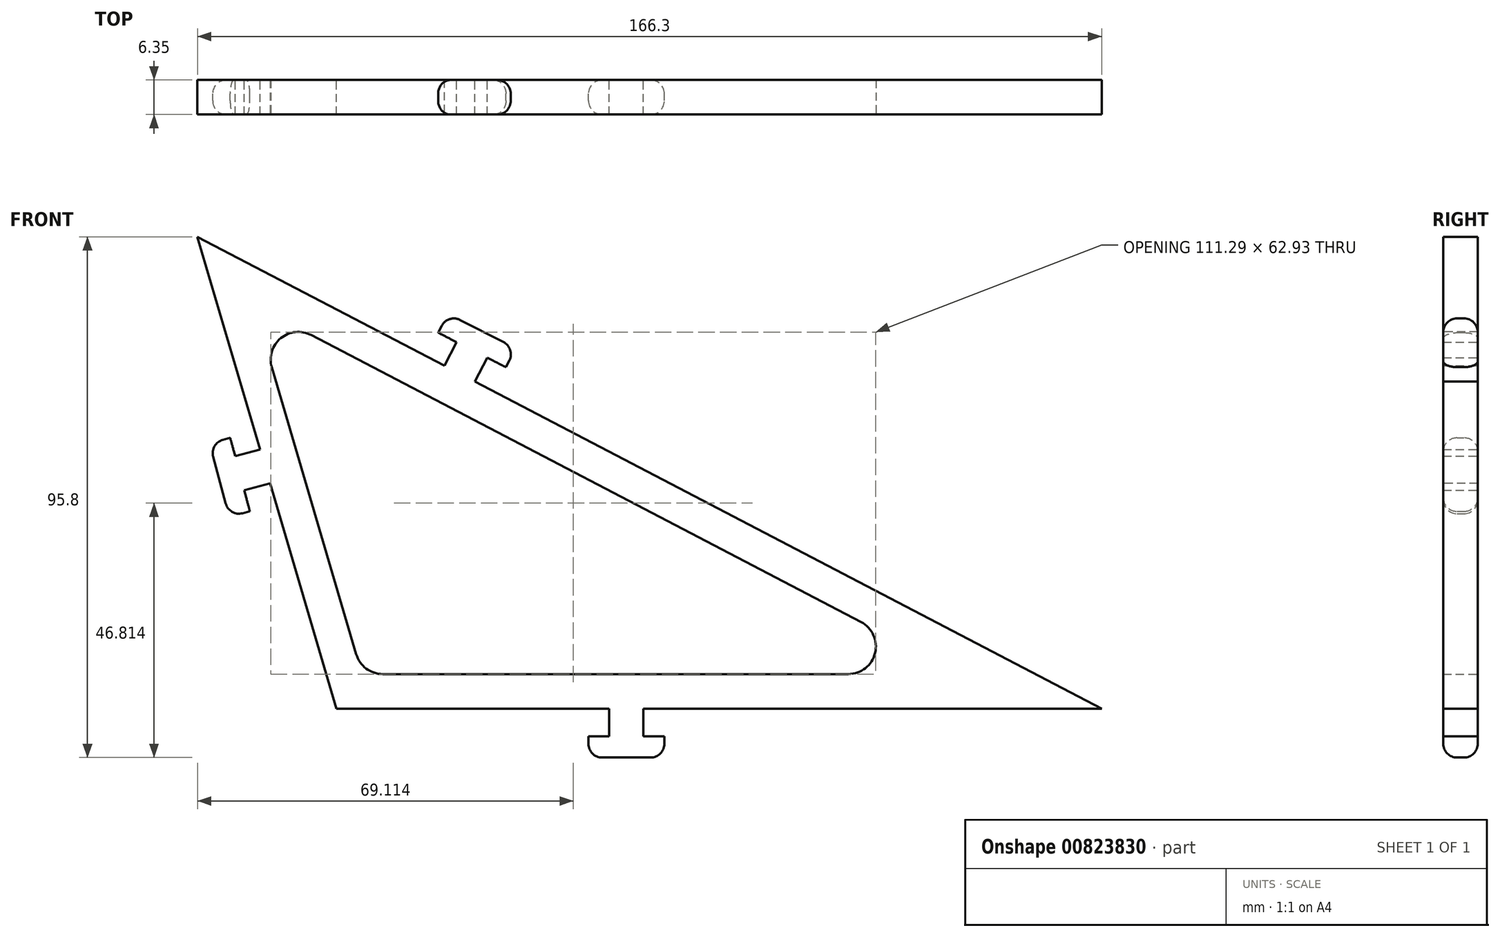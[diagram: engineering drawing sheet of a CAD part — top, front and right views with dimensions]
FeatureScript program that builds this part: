
annotation { "Feature Type Name" : "Feature", "Feature Type Description" : "" }
export const myFeature = defineFeature(function(context is Context, id is Id, definition is map)
    precondition{}
    {
        {
            var Q0;
            Q0=qCreatedBy(makeId("Front.planeOp"),FACE);
            var sketch = newSketch(context, id + "F0", { "sketchPlane" : qUnion([Q0])});
            skLineSegment(sketch, "E0", {"start": v(0, 0) * mm, "end": v(-140.78, 0) * mm});
            skLineSegment(sketch, "E1", {"start": v(-140.78, 0) * mm, "end": v(-166.3, 86.8) * mm});
            skLineSegment(sketch, "E2", {"start": v(-166.3, 86.8) * mm, "end": v(0, 0) * mm});
            skLineSegment(sketch, "E3.0", {"start": v(-156, 74.26) * mm, "end": v(-25.89, 6.35) * mm});
            skLineSegment(sketch, "E3.1", {"start": v(-136.03, 6.35) * mm, "end": v(-156, 74.26) * mm});
            skLineSegment(sketch, "E3.2", {"start": v(-25.89, 6.35) * mm, "end": v(-136.03, 6.35) * mm});
            skSolve(sketch);
        }
        {
            var Q0;
            Q0 = qSketchRegion(id + "F0", true);
            extrude(context, id + "F1", {"entities" : qUnion([Q0]), "depth" : 6.35 * mm, "offsetDistance" : 25.4 * mm});
        }
        {
            var Q0;
            Q0=makeQuery(id+"F1.opExtrude","SWEPT_EDGE",EDGE,{"disambiguationData":[OSD([sQuery(id+"F0.wireOp",EDGE,"E3.0"),sQuery(id+"F0.wireOp",EDGE,"E3.1")])]});
            var Q1;
            Q1=makeQuery(id+"F1.opExtrude","SWEPT_EDGE",EDGE,{"disambiguationData":[OSD([sQuery(id+"F0.wireOp",EDGE,"E3.0"),sQuery(id+"F0.wireOp",EDGE,"E3.2")])]});
            var Q2;
            Q2=makeQuery(id+"F1.opExtrude","SWEPT_EDGE",EDGE,{"disambiguationData":[OSD([sQuery(id+"F0.wireOp",EDGE,"E3.1"),sQuery(id+"F0.wireOp",EDGE,"E3.2")])]});
            fillet(context, id + "F2", {"entities" : qUnion([Q0, Q1, Q2]), "radius" : 5.08 * mm, "tangentPropagation" : true, "allowEdgeOverflow" : false});
        }
        {
            var Q0;
            Q0=qCreatedBy(makeId("Front.planeOp"),FACE);
            var sketch = newSketch(context, id + "F3", { "sketchPlane" : qUnion([Q0])});
            skLineSegment(sketch, "E4", {"start": v(-90.6, 0) * mm, "end": v(-90.6, -5.08) * mm});
            skLineSegment(sketch, "E5", {"start": v(-90.6, -5.08) * mm, "end": v(-94.4, -5.08) * mm});
            skLineSegment(sketch, "E6", {"start": v(-94.4, -5.08) * mm, "end": v(-94.4, -9) * mm});
            skLineSegment(sketch, "E7", {"start": v(-94.4, -9) * mm, "end": v(-80.42, -9) * mm});
            skLineSegment(sketch, "E8", {"start": v(-80.42, -9) * mm, "end": v(-80.42, -5.08) * mm});
            skLineSegment(sketch, "E9", {"start": v(-80.42, -5.08) * mm, "end": v(-84.3, -5.08) * mm});
            skLineSegment(sketch, "E10", {"start": v(-84.3, -5.08) * mm, "end": v(-84.3, 0) * mm});
            skLineSegment(sketch, "E11", {"start": v(-84.3, 0) * mm, "end": v(-90.6, 0) * mm});
            skSolve(sketch);
        }
        {
            var Q0;
            Q0=makeQuery(id+"F3.imprint","IMPRINT",FACE,{"disambiguationData":[TD([[makeQuery(id+"F3.imprint","IMPRINT",EDGE,{"derivedFrom":sQuery(id+"F3.wireOp",EDGE,"E4")}),1.0]])]});
            extrude(context, id + "F4", {"entities" : qUnion([Q0]), "operationType" : NewBodyOperationType.ADD, "depth" : 6.35 * mm, "offsetDistance" : 25.4 * mm});
        }
        {
            var Q0;
            Q0=makeQuery(id+"F4.opExtrude","CAP_EDGE",EDGE,{"disambiguationData":[OSD([sQuery(id+"F3.wireOp",EDGE,"E8")])],"isStart":true});
            fillet(context, id + "F5", {"entities" : qUnion([Q0]), "radius" : 2.54 * mm, "tangentPropagation" : true, "allowEdgeOverflow" : false});
        }
        {
            var Q0;
            Q0=makeQuery(id+"F4.opExtrude","CAP_EDGE",EDGE,{"disambiguationData":[OSD([sQuery(id+"F3.wireOp",EDGE,"E6")])],"isStart":true});
            fillet(context, id + "F6", {"entities" : qUnion([Q0]), "radius" : 2.54 * mm, "tangentPropagation" : true, "allowEdgeOverflow" : false});
        }
        {
            var Q0;
            Q0=makeQuery(id+"F4.opExtrude","CAP_EDGE",EDGE,{"disambiguationData":[OSD([sQuery(id+"F3.wireOp",EDGE,"E6")])],"isStart":false});
            var Q1;
            Q1=makeQuery(id+"F4.opExtrude","CAP_EDGE",EDGE,{"disambiguationData":[OSD([sQuery(id+"F3.wireOp",EDGE,"E8")])],"isStart":false});
            fillet(context, id + "F7", {"entities" : qUnion([Q0, Q1]), "radius" : 2.54 * mm, "tangentPropagation" : true, "allowEdgeOverflow" : false});
        }
        {
            var Q0;
            Q0=makeQuery(id+"F4.opExtrude","CAP_EDGE",EDGE,{"disambiguationData":[OSD([sQuery(id+"F3.wireOp",EDGE,"E7")])],"isStart":false});
            var Q1;
            Q1=makeQuery(id+"F4.opExtrude","CAP_EDGE",EDGE,{"disambiguationData":[OSD([sQuery(id+"F3.wireOp",EDGE,"E7")])],"isStart":true});
            fillet(context, id + "F8", {"entities" : qUnion([Q0, Q1]), "radius" : 2.54 * mm, "tangentPropagation" : true, "allowEdgeOverflow" : false});
        }
        {
            var Q0;
            Q0=makeQuery(id+"F4.boolean.opBoolean","MERGE",FACE,{"derivedFrom":[makeQuery(id+"F1.opExtrude","CAP_FACE",FACE,{"disambiguationData":[OSD([sQuery(id+"F0.wireOp",EDGE,"E0"),sQuery(id+"F0.wireOp",EDGE,"E1"),sQuery(id+"F0.wireOp",EDGE,"E2"),sQuery(id+"F0.wireOp",EDGE,"E3.0"),sQuery(id+"F0.wireOp",EDGE,"E3.1"),sQuery(id+"F0.wireOp",EDGE,"E3.2")])],"isStart":true}),makeQuery(id+"F4.opExtrude","CAP_FACE",FACE,{"disambiguationData":[OSD([sQuery(id+"F3.wireOp",EDGE,"E4"),sQuery(id+"F3.wireOp",EDGE,"E5"),sQuery(id+"F3.wireOp",EDGE,"E6"),sQuery(id+"F3.wireOp",EDGE,"E7"),sQuery(id+"F3.wireOp",EDGE,"E8"),sQuery(id+"F3.wireOp",EDGE,"E9"),sQuery(id+"F3.wireOp",EDGE,"E10"),sQuery(id+"F3.wireOp",EDGE,"E11")])],"isStart":true})]});
            var sketch = newSketch(context, id + "F9", { "sketchPlane" : qUnion([Q0])});
            skLineSegment(sketch, "E12", {"start": v(152.92, 41.46) * mm, "end": v(157.7, 40.18) * mm});
            skLineSegment(sketch, "E13", {"start": v(157.7, 40.18) * mm, "end": v(156.66, 36.3) * mm});
            skLineSegment(sketch, "E14", {"start": v(156.66, 36.3) * mm, "end": v(160.45, 35.29) * mm});
            skLineSegment(sketch, "E15", {"start": v(160.45, 35.29) * mm, "end": v(164.07, 48.8) * mm});
            skLineSegment(sketch, "E16", {"start": v(164.07, 48.8) * mm, "end": v(160.28, 49.81) * mm});
            skLineSegment(sketch, "E17", {"start": v(160.28, 49.81) * mm, "end": v(159.38, 46.45) * mm});
            skLineSegment(sketch, "E18", {"start": v(159.38, 46.45) * mm, "end": v(154.6, 47.73) * mm});
            skLineSegment(sketch, "E19", {"start": v(154.6, 47.73) * mm, "end": v(152.92, 41.46) * mm});
            skLineSegment(sketch, "E20.0", {"start": v(157.7, 40.18) * mm, "end": v(160.28, 49.81) * mm, "construction": true});
            skSolve(sketch);
        }
        {
            var Q0;
            {var subQ0=sQuery(id+"F9.wireOp",EDGE,"E19");Q0=makeQuery(id+"F9.imprint","IMPRINT",FACE,{"disambiguationData":[TD([[makeQuery(id+"F9.imprint","IMPRINT",EDGE,{"derivedFrom":subQ0}),1.0]])]});}
            var Q1;
            {var subQ0=sQuery(id+"F9.wireOp",EDGE,"E13");Q1=makeQuery(id+"F9.imprint","IMPRINT",FACE,{"disambiguationData":[TD([[makeQuery(id+"F9.imprint","IMPRINT",EDGE,{"derivedFrom":subQ0}),1.0]])]});}
            extrude(context, id + "F10", {"entities" : qUnion([Q0, Q1]), "operationType" : NewBodyOperationType.ADD, "oppositeDirection" : true, "depth" : 6.35 * mm, "offsetDistance" : 25.4 * mm});
        }
        {
            var Q0;
            Q0=makeQuery(id+"F10.opExtrude","CAP_EDGE",EDGE,{"disambiguationData":[OSD([sQuery(id+"F9.wireOp",EDGE,"E16")])],"isStart":false});
            var Q1;
            Q1=makeQuery(id+"F10.opExtrude","CAP_EDGE",EDGE,{"disambiguationData":[OSD([sQuery(id+"F9.wireOp",EDGE,"E14")])],"isStart":false});
            fillet(context, id + "F11", {"entities" : qUnion([Q0, Q1]), "radius" : 2.54 * mm, "tangentPropagation" : true, "allowEdgeOverflow" : false});
        }
        {
            var Q0;
            Q0=makeQuery(id+"F10.opExtrude","CAP_EDGE",EDGE,{"disambiguationData":[OSD([sQuery(id+"F9.wireOp",EDGE,"E16")])],"isStart":true});
            var Q1;
            Q1=makeQuery(id+"F10.opExtrude","CAP_EDGE",EDGE,{"disambiguationData":[OSD([sQuery(id+"F9.wireOp",EDGE,"E14")])],"isStart":true});
            fillet(context, id + "F12", {"entities" : qUnion([Q0, Q1]), "radius" : 2.54 * mm, "tangentPropagation" : true, "allowEdgeOverflow" : false});
        }
        {
            var Q0;
            Q0=makeQuery(id+"F10.opExtrude","CAP_EDGE",EDGE,{"disambiguationData":[OSD([sQuery(id+"F9.wireOp",EDGE,"E15")])],"isStart":true});
            var Q1;
            Q1=makeQuery(id+"F12.opFillet","BLEND_EDGE",EDGE,{"blendedFrom":[makeQuery(id+"F10.opExtrude","CAP_EDGE",EDGE,{"disambiguationData":[OSD([sQuery(id+"F9.wireOp",EDGE,"E16")])],"isStart":true}),makeQuery(id+"F10.opExtrude","SWEPT_FACE",FACE,{"disambiguationData":[OSD([sQuery(id+"F9.wireOp",EDGE,"E15")])]})],"blendedInto":[makeQuery(id+"F10.opExtrude","SWEPT_FACE",FACE,{"disambiguationData":[OSD([sQuery(id+"F9.wireOp",EDGE,"E15")])]})]});
            var Q2;
            Q2=makeQuery(id+"F11.opFillet","BLEND_EDGE",EDGE,{"blendedFrom":[makeQuery(id+"F10.opExtrude","CAP_EDGE",EDGE,{"disambiguationData":[OSD([sQuery(id+"F9.wireOp",EDGE,"E16")])],"isStart":false}),makeQuery(id+"F10.opExtrude","SWEPT_FACE",FACE,{"disambiguationData":[OSD([sQuery(id+"F9.wireOp",EDGE,"E15")])]})],"blendedInto":[makeQuery(id+"F10.opExtrude","SWEPT_FACE",FACE,{"disambiguationData":[OSD([sQuery(id+"F9.wireOp",EDGE,"E15")])]})]});
            var Q3;
            Q3=makeQuery(id+"F10.opExtrude","CAP_EDGE",EDGE,{"disambiguationData":[OSD([sQuery(id+"F9.wireOp",EDGE,"E15")])],"isStart":false});
            var Q4;
            Q4=makeQuery(id+"F11.opFillet","BLEND_EDGE",EDGE,{"blendedFrom":[makeQuery(id+"F10.opExtrude","CAP_EDGE",EDGE,{"disambiguationData":[OSD([sQuery(id+"F9.wireOp",EDGE,"E14")])],"isStart":false}),makeQuery(id+"F10.opExtrude","SWEPT_FACE",FACE,{"disambiguationData":[OSD([sQuery(id+"F9.wireOp",EDGE,"E15")])]})],"blendedInto":[makeQuery(id+"F10.opExtrude","SWEPT_FACE",FACE,{"disambiguationData":[OSD([sQuery(id+"F9.wireOp",EDGE,"E15")])]})]});
            var Q5;
            Q5=makeQuery(id+"F12.opFillet","BLEND_EDGE",EDGE,{"blendedFrom":[makeQuery(id+"F10.opExtrude","CAP_EDGE",EDGE,{"disambiguationData":[OSD([sQuery(id+"F9.wireOp",EDGE,"E14")])],"isStart":true}),makeQuery(id+"F10.opExtrude","SWEPT_FACE",FACE,{"disambiguationData":[OSD([sQuery(id+"F9.wireOp",EDGE,"E15")])]})],"blendedInto":[makeQuery(id+"F10.opExtrude","SWEPT_FACE",FACE,{"disambiguationData":[OSD([sQuery(id+"F9.wireOp",EDGE,"E15")])]})]});
            fillet(context, id + "F13", {"entities" : qUnion([Q0, Q1, Q2, Q3, Q4, Q5]), "radius" : 2.54 * mm, "tangentPropagation" : true, "allowEdgeOverflow" : false});
        }
        {
            var Q0;
            Q0=makeQuery(id+"F10.boolean.opBoolean","MERGE",FACE,{"derivedFrom":[makeQuery(id+"F4.boolean.opBoolean","MERGE",FACE,{"derivedFrom":[makeQuery(id+"F1.opExtrude","CAP_FACE",FACE,{"disambiguationData":[OSD([sQuery(id+"F0.wireOp",EDGE,"E0"),sQuery(id+"F0.wireOp",EDGE,"E1"),sQuery(id+"F0.wireOp",EDGE,"E2"),sQuery(id+"F0.wireOp",EDGE,"E3.0"),sQuery(id+"F0.wireOp",EDGE,"E3.1"),sQuery(id+"F0.wireOp",EDGE,"E3.2")])],"isStart":true}),makeQuery(id+"F4.opExtrude","CAP_FACE",FACE,{"disambiguationData":[OSD([sQuery(id+"F3.wireOp",EDGE,"E4"),sQuery(id+"F3.wireOp",EDGE,"E5"),sQuery(id+"F3.wireOp",EDGE,"E6"),sQuery(id+"F3.wireOp",EDGE,"E7"),sQuery(id+"F3.wireOp",EDGE,"E8"),sQuery(id+"F3.wireOp",EDGE,"E9"),sQuery(id+"F3.wireOp",EDGE,"E10"),sQuery(id+"F3.wireOp",EDGE,"E11")])],"isStart":true})]}),makeQuery(id+"F10.opExtrude","CAP_FACE",FACE,{"disambiguationData":[OSD([sQuery(id+"F9.wireOp",EDGE,"E12"),sQuery(id+"F9.wireOp",EDGE,"E13"),sQuery(id+"F9.wireOp",EDGE,"E14"),sQuery(id+"F9.wireOp",EDGE,"E15"),sQuery(id+"F9.wireOp",EDGE,"E16"),sQuery(id+"F9.wireOp",EDGE,"E17"),sQuery(id+"F9.wireOp",EDGE,"E18"),sQuery(id+"F9.wireOp",EDGE,"E19")])],"isStart":true})]});
            var sketch = newSketch(context, id + "F14", { "sketchPlane" : qUnion([Q0])});
            skLineSegment(sketch, "E21", {"start": v(120.94, 62.9) * mm, "end": v(118.64, 67.44) * mm});
            skLineSegment(sketch, "E22", {"start": v(118.64, 67.44) * mm, "end": v(122.03, 69.17) * mm});
            skLineSegment(sketch, "E23", {"start": v(122.03, 69.17) * mm, "end": v(120.25, 72.66) * mm});
            skLineSegment(sketch, "E24", {"start": v(120.25, 72.66) * mm, "end": v(107.79, 66.3) * mm});
            skLineSegment(sketch, "E25", {"start": v(107.79, 66.3) * mm, "end": v(109.57, 62.81) * mm});
            skLineSegment(sketch, "E26", {"start": v(109.57, 62.81) * mm, "end": v(113.03, 64.58) * mm});
            skLineSegment(sketch, "E27", {"start": v(113.03, 64.58) * mm, "end": v(115.34, 60.05) * mm});
            skLineSegment(sketch, "E28", {"start": v(115.34, 60.05) * mm, "end": v(120.94, 62.9) * mm});
            skLineSegment(sketch, "E29.0", {"start": v(118.64, 67.44) * mm, "end": v(109.57, 62.81) * mm, "construction": true});
            skSolve(sketch);
        }
        {
            var Q0;
            {var subQ5=sQuery(id+"F14.wireOp",EDGE,"E22");Q0=makeQuery(id+"F14.imprint","IMPRINT",FACE,{"disambiguationData":[TD([[makeQuery(id+"F14.imprint","IMPRINT",EDGE,{"derivedFrom":subQ5}),1.0]])]});}
            extrude(context, id + "F15", {"entities" : qUnion([Q0]), "operationType" : NewBodyOperationType.ADD, "oppositeDirection" : true, "depth" : 6.35 * mm, "offsetDistance" : 25.4 * mm});
        }
        {
            var Q0;
            Q0=makeQuery(id+"F15.opExtrude","CAP_EDGE",EDGE,{"disambiguationData":[OSD([sQuery(id+"F14.wireOp",EDGE,"E24")])],"isStart":false});
            var Q1;
            Q1=makeQuery(id+"F15.opExtrude","CAP_EDGE",EDGE,{"disambiguationData":[OSD([sQuery(id+"F14.wireOp",EDGE,"E24")])],"isStart":true});
            fillet(context, id + "F16", {"entities" : qUnion([Q0, Q1]), "radius" : 2.54 * mm, "tangentPropagation" : true, "allowEdgeOverflow" : false});
        }
        {
            var Q0;
            Q0=makeQuery(id+"F16.opFillet","BLEND_EDGE",EDGE,{"blendedFrom":[makeQuery(id+"F15.opExtrude","CAP_EDGE",EDGE,{"disambiguationData":[OSD([sQuery(id+"F14.wireOp",EDGE,"E24")])],"isStart":true}),makeQuery(id+"F15.opExtrude","SWEPT_FACE",FACE,{"disambiguationData":[OSD([sQuery(id+"F14.wireOp",EDGE,"E23")])]})],"blendedInto":[makeQuery(id+"F15.opExtrude","SWEPT_FACE",FACE,{"disambiguationData":[OSD([sQuery(id+"F14.wireOp",EDGE,"E23")])]})]});
            var Q1;
            Q1=makeQuery(id+"F16.opFillet","BLEND_EDGE",EDGE,{"blendedFrom":[makeQuery(id+"F15.opExtrude","CAP_EDGE",EDGE,{"disambiguationData":[OSD([sQuery(id+"F14.wireOp",EDGE,"E24")])],"isStart":false}),makeQuery(id+"F15.opExtrude","SWEPT_FACE",FACE,{"disambiguationData":[OSD([sQuery(id+"F14.wireOp",EDGE,"E23")])]})],"blendedInto":[makeQuery(id+"F15.opExtrude","SWEPT_FACE",FACE,{"disambiguationData":[OSD([sQuery(id+"F14.wireOp",EDGE,"E23")])]})]});
            var Q2;
            Q2=makeQuery(id+"F15.opExtrude","SWEPT_EDGE",EDGE,{"disambiguationData":[OSD([sQuery(id+"F14.wireOp",EDGE,"E23"),sQuery(id+"F14.wireOp",EDGE,"E24")])]});
            var Q3;
            Q3=makeQuery(id+"F15.opExtrude","CAP_EDGE",EDGE,{"disambiguationData":[OSD([sQuery(id+"F14.wireOp",EDGE,"E23")])],"isStart":false});
            fillet(context, id + "F17", {"entities" : qUnion([Q0, Q1, Q2, Q3]), "radius" : 2.54 * mm, "tangentPropagation" : true, "allowEdgeOverflow" : false});
        }
        {
            var Q0;
            Q0=makeQuery(id+"F16.opFillet","BLEND_EDGE",EDGE,{"blendedFrom":[makeQuery(id+"F15.opExtrude","CAP_EDGE",EDGE,{"disambiguationData":[OSD([sQuery(id+"F14.wireOp",EDGE,"E24")])],"isStart":true}),makeQuery(id+"F15.opExtrude","SWEPT_FACE",FACE,{"disambiguationData":[OSD([sQuery(id+"F14.wireOp",EDGE,"E25")])]})],"blendedInto":[makeQuery(id+"F15.opExtrude","SWEPT_FACE",FACE,{"disambiguationData":[OSD([sQuery(id+"F14.wireOp",EDGE,"E25")])]})]});
            var Q1;
            Q1=makeQuery(id+"F15.opExtrude","CAP_EDGE",EDGE,{"disambiguationData":[OSD([sQuery(id+"F14.wireOp",EDGE,"E25")])],"isStart":true});
            var Q2;
            Q2=makeQuery(id+"F15.opExtrude","CAP_EDGE",EDGE,{"disambiguationData":[OSD([sQuery(id+"F14.wireOp",EDGE,"E25")])],"isStart":false});
            var Q3;
            Q3=makeQuery(id+"F16.opFillet","BLEND_EDGE",EDGE,{"blendedFrom":[makeQuery(id+"F15.opExtrude","CAP_EDGE",EDGE,{"disambiguationData":[OSD([sQuery(id+"F14.wireOp",EDGE,"E24")])],"isStart":false}),makeQuery(id+"F15.opExtrude","SWEPT_FACE",FACE,{"disambiguationData":[OSD([sQuery(id+"F14.wireOp",EDGE,"E25")])]})],"blendedInto":[makeQuery(id+"F15.opExtrude","SWEPT_FACE",FACE,{"disambiguationData":[OSD([sQuery(id+"F14.wireOp",EDGE,"E25")])]})]});
            fillet(context, id + "F18", {"entities" : qUnion([Q0, Q1, Q2, Q3]), "radius" : 2.54 * mm, "tangentPropagation" : true, "allowEdgeOverflow" : false});
        }
    });
